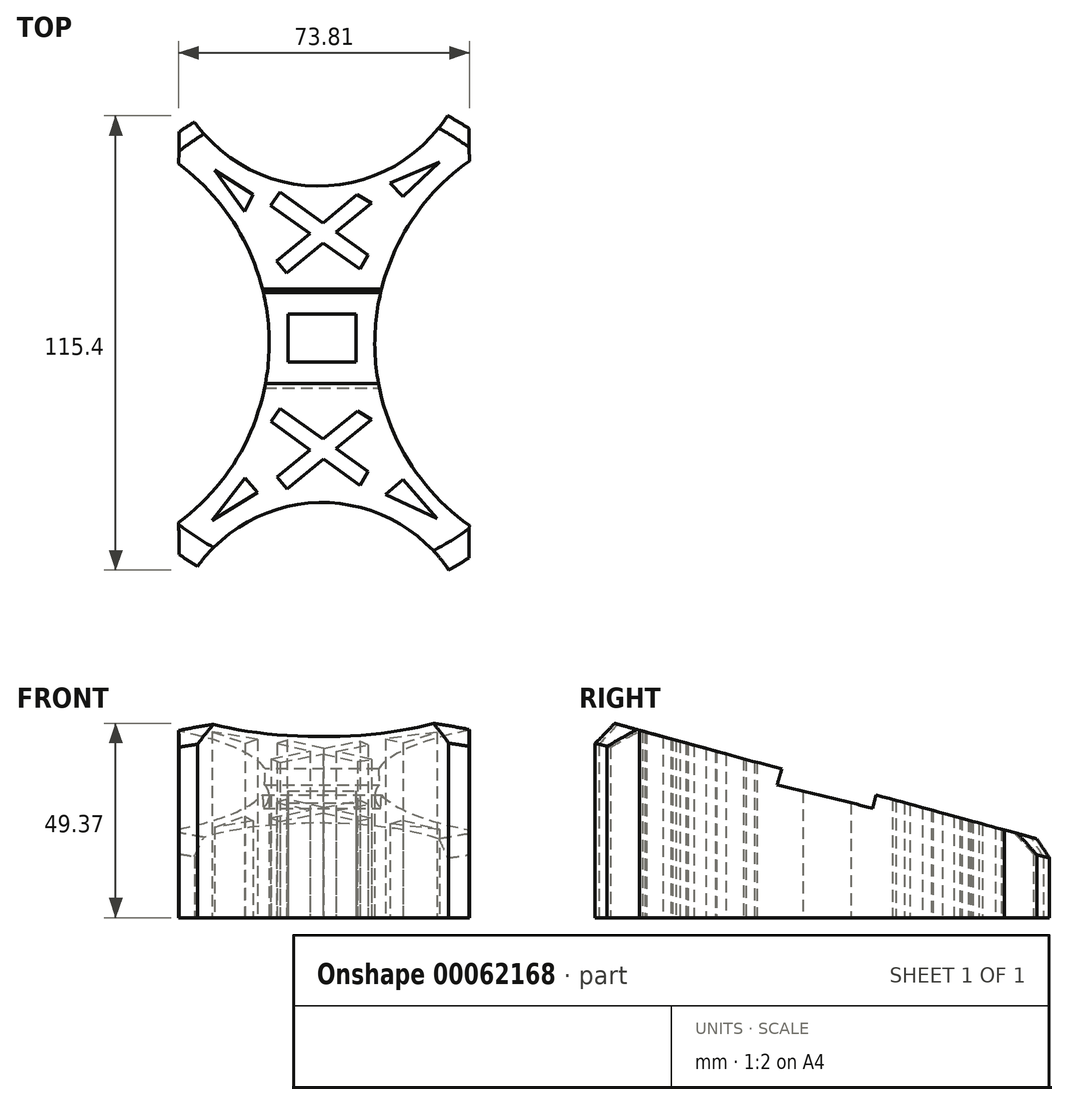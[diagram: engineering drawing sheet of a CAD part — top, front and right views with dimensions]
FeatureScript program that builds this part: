
annotation { "Feature Type Name" : "Feature", "Feature Type Description" : "" }
export const myFeature = defineFeature(function(context is Context, id is Id, definition is map)
    precondition{}
    {
        {
            var Q0;
            Q0=qCreatedBy(makeId("Top.planeOp"),FACE);
            var sketch = newSketch(context, id + "F0", { "sketchPlane" : qUnion([Q0])});
            skArc(sketch, "E0", {"start": v(-115.94, 56.2) * mm, "mid": v(-120.89, 52.92) * mm, "end": v(-125.52, 49.22) * mm});
            skArc(sketch, "E1", {"start": v(-40.14, 50) * mm, "mid": v(-70.11, 0) * mm, "end": v(-40.14, -50) * mm});
            skArc(sketch, "E2", {"start": v(-125.52, -49.22) * mm, "mid": v(-96.95, 0) * mm, "end": v(-125.52, 49.22) * mm});
            skArc(sketch, "E3", {"start": v(-115.94, 56.2) * mm, "mid": v(-83.36, 39.87) * mm, "end": v(-51.62, 57.78) * mm});
            skArc(sketch, "E4", {"start": v(-51.33, -57.62) * mm, "mid": v(-82.97, -40.44) * mm, "end": v(-115.1, -56.68) * mm});
            skArc(sketch, "E5.trimOffspring", {"start": v(-40.14, 50) * mm, "mid": v(-45.67, 54.2) * mm, "end": v(-51.62, 57.78) * mm});
            skArc(sketch, "E6.trimOffspring", {"start": v(-125.52, -49.22) * mm, "mid": v(-120.5, -53.2) * mm, "end": v(-115.1, -56.68) * mm});
            skArc(sketch, "E7.trimOffspring", {"start": v(-51.33, -57.62) * mm, "mid": v(-45.54, -54.1) * mm, "end": v(-40.14, -50) * mm});
            skSolve(sketch);
        }
        {
            var Q0;
            Q0 = qSketchRegion(id + "F0", true);
            extrude(context, id + "F1", {"entities" : qUnion([Q0]), "depth" : 50 * mm});
        }
        {
            var Q0;
            Q0=qCreatedBy(makeId("Right.planeOp"),FACE);
            var sketch = newSketch(context, id + "F2", { "sketchPlane" : qUnion([Q0])});
            skLineSegment(sketch, "E8", {"start": v(-59.85, 51.33) * mm, "end": v(61.8, 18.07) * mm});
            skLineSegment(sketch, "E9", {"start": v(61.8, 18.07) * mm, "end": v(61.8, 52.6) * mm});
            skLineSegment(sketch, "E10", {"start": v(61.8, 52.6) * mm, "end": v(-59.85, 51.33) * mm});
            skSolve(sketch);
        }
        {
            var Q0;
            Q0 = qSketchRegion(id + "F2", true);
            extrude(context, id + "F3", {"entities" : qUnion([Q0]), "operationType" : NewBodyOperationType.REMOVE, "endBound" : BoundingType.THROUGH_ALL, "oppositeDirection" : true, "depth" : 25 * mm});
        }
        {
            var Q0;
            Q0=qCreatedBy(makeId("Right.planeOp"),FACE);
            var sketch = newSketch(context, id + "F4", { "sketchPlane" : qUnion([Q0])});
            skLineSegment(sketch, "E11", {"start": v(-11.4, 33.8) * mm, "end": v(12.88, 27.84) * mm});
            skLineSegment(sketch, "E12", {"start": v(12.88, 27.84) * mm, "end": v(14.86, 35.9) * mm});
            skLineSegment(sketch, "E13", {"start": v(14.86, 35.9) * mm, "end": v(-9.04, 41.78) * mm});
            skLineSegment(sketch, "E14", {"start": v(-9.04, 41.78) * mm, "end": v(-11.4, 33.8) * mm});
            skSolve(sketch);
        }
        {
            var Q0;
            Q0 = qSketchRegion(id + "F4", true);
            extrude(context, id + "F5", {"entities" : qUnion([Q0]), "operationType" : NewBodyOperationType.REMOVE, "endBound" : BoundingType.THROUGH_ALL, "oppositeDirection" : true, "depth" : 25 * mm});
        }
        {
            var Q0;
            Q0=makeQuery(id+"F3.boolean.opBoolean","INTERSECT",EDGE,{"derivedFrom":[makeQuery(id+"F1.opExtrude","SWEPT_FACE",FACE,{"disambiguationData":[OSD([sQuery(id+"F0.wireOp",EDGE,"E0")])]}),makeQuery(id+"F3.opExtrude","SWEPT_FACE",FACE,{"disambiguationData":[OSD([sQuery(id+"F2.wireOp",EDGE,"E8")])]})]});
            var Q1;
            Q1=makeQuery(id+"F3.boolean.opBoolean","INTERSECT",EDGE,{"derivedFrom":[makeQuery(id+"F1.opExtrude","SWEPT_FACE",FACE,{"disambiguationData":[OSD([sQuery(id+"F0.wireOp",EDGE,"E5.trimOffspring")])]}),makeQuery(id+"F3.opExtrude","SWEPT_FACE",FACE,{"disambiguationData":[OSD([sQuery(id+"F2.wireOp",EDGE,"E8")])]})]});
            var Q2;
            Q2=makeQuery(id+"F3.boolean.opBoolean","INTERSECT",EDGE,{"derivedFrom":[makeQuery(id+"F1.opExtrude","SWEPT_FACE",FACE,{"disambiguationData":[OSD([sQuery(id+"F0.wireOp",EDGE,"E7.trimOffspring")])]}),makeQuery(id+"F3.opExtrude","SWEPT_FACE",FACE,{"disambiguationData":[OSD([sQuery(id+"F2.wireOp",EDGE,"E8")])]})]});
            var Q3;
            Q3=makeQuery(id+"F3.boolean.opBoolean","INTERSECT",EDGE,{"derivedFrom":[makeQuery(id+"F1.opExtrude","SWEPT_FACE",FACE,{"disambiguationData":[OSD([sQuery(id+"F0.wireOp",EDGE,"E6.trimOffspring")])]}),makeQuery(id+"F3.opExtrude","SWEPT_FACE",FACE,{"disambiguationData":[OSD([sQuery(id+"F2.wireOp",EDGE,"E8")])]})]});
            var Q4;
            Q4=makeQuery(id+"F1.opExtrude","SWEPT_EDGE",EDGE,{"disambiguationData":[OSD([sQuery(id+"F0.wireOp",EDGE,"E1"),sQuery(id+"F0.wireOp",EDGE,"E7.trimOffspring")])]});
            var Q5;
            Q5=makeQuery(id+"F1.opExtrude","SWEPT_EDGE",EDGE,{"disambiguationData":[OSD([sQuery(id+"F0.wireOp",EDGE,"E2"),sQuery(id+"F0.wireOp",EDGE,"E6.trimOffspring")])]});
            var Q6;
            Q6=makeQuery(id+"F1.opExtrude","SWEPT_EDGE",EDGE,{"disambiguationData":[OSD([sQuery(id+"F0.wireOp",EDGE,"E0"),sQuery(id+"F0.wireOp",EDGE,"E2")])]});
            var Q7;
            Q7=makeQuery(id+"F1.opExtrude","SWEPT_EDGE",EDGE,{"disambiguationData":[OSD([sQuery(id+"F0.wireOp",EDGE,"E1"),sQuery(id+"F0.wireOp",EDGE,"E5.trimOffspring")])]});
            chamfer(context, id + "F6", {"entities" : qUnion([Q0, Q1, Q2, Q3, Q4, Q5, Q6, Q7]), "width" : 5 * mm, "tangentPropagation" : true});
        }
        {
            var Q0;
            Q0=qCreatedBy(makeId("Top.planeOp"),FACE);
            var sketch = newSketch(context, id + "F7", { "sketchPlane" : qUnion([Q0])});
            skLineSegment(sketch, "E15.bottom", {"start": v(-92.17, 7.35) * mm, "end": v(-74.88, 7.35) * mm});
            skLineSegment(sketch, "E15.top", {"start": v(-92.17, -4.83) * mm, "end": v(-74.88, -4.83) * mm});
            skLineSegment(sketch, "E15.left", {"start": v(-92.17, 7.35) * mm, "end": v(-92.17, -4.83) * mm});
            skLineSegment(sketch, "E15.right", {"start": v(-74.88, 7.35) * mm, "end": v(-74.88, -4.83) * mm});
            skLineSegment(sketch, "E16", {"start": v(-96.58, 35) * mm, "end": v(-86.58, 27.85) * mm});
            skLineSegment(sketch, "E17", {"start": v(-71, 35.6) * mm, "end": v(-79.98, 28.17) * mm});
            skLineSegment(sketch, "E18", {"start": v(-92.49, 17.82) * mm, "end": v(-95.01, 20.88) * mm});
            skLineSegment(sketch, "E19", {"start": v(-95.01, 20.88) * mm, "end": v(-86.58, 27.85) * mm});
            skLineSegment(sketch, "E20", {"start": v(-74.62, 37.75) * mm, "end": v(-71, 35.6) * mm});
            skLineSegment(sketch, "E21", {"start": v(-96.58, 35) * mm, "end": v(-94.2, 38.34) * mm});
            skLineSegment(sketch, "E22", {"start": v(-94.2, 38.34) * mm, "end": v(-83.32, 30.55) * mm});
            skLineSegment(sketch, "E23", {"start": v(-71.86, 22.36) * mm, "end": v(-73.92, 18.8) * mm});
            skLineSegment(sketch, "E24.trimOffspring", {"start": v(-83.32, 30.55) * mm, "end": v(-74.62, 37.75) * mm});
            skLineSegment(sketch, "E25.trimOffspring", {"start": v(-79.98, 28.17) * mm, "end": v(-71.86, 22.36) * mm});
            skLineSegment(sketch, "E26.trimOffspring", {"start": v(-83.25, 25.46) * mm, "end": v(-92.49, 17.82) * mm});
            skLineSegment(sketch, "E27.trimOffspring", {"start": v(-83.25, 25.46) * mm, "end": v(-73.92, 18.8) * mm});
            skLineSegment(sketch, "E28", {"start": v(-70.93, -19.34) * mm, "end": v(-79.9, -26.77) * mm});
            skLineSegment(sketch, "E29.trimOffspring", {"start": v(-83.24, -24.38) * mm, "end": v(-74.54, -17.18) * mm});
            skLineSegment(sketch, "E30.trimOffspring", {"start": v(-83.18, -29.47) * mm, "end": v(-92.41, -37.11) * mm});
            skLineSegment(sketch, "E31.trimOffspring", {"start": v(-83.18, -29.47) * mm, "end": v(-73.85, -36.14) * mm});
            skLineSegment(sketch, "E32", {"start": v(-94.12, -16.6) * mm, "end": v(-83.24, -24.38) * mm});
            skLineSegment(sketch, "E33", {"start": v(-96.51, -19.93) * mm, "end": v(-86.51, -27.08) * mm});
            skLineSegment(sketch, "E34.trimOffspring", {"start": v(-79.9, -26.77) * mm, "end": v(-71.79, -32.58) * mm});
            skLineSegment(sketch, "E35", {"start": v(-94.94, -34.06) * mm, "end": v(-86.51, -27.08) * mm});
            skLineSegment(sketch, "E36", {"start": v(-96.51, -19.93) * mm, "end": v(-94.12, -16.6) * mm});
            skLineSegment(sketch, "E37", {"start": v(-92.41, -37.11) * mm, "end": v(-94.94, -34.06) * mm});
            skLineSegment(sketch, "E38", {"start": v(-71.79, -32.58) * mm, "end": v(-73.85, -36.14) * mm});
            skLineSegment(sketch, "E39", {"start": v(-74.54, -17.18) * mm, "end": v(-70.93, -19.34) * mm});
            skLineSegment(sketch, "E40", {"start": v(-110.82, 44.01) * mm, "end": v(-103.22, 33.5) * mm});
            skLineSegment(sketch, "E41", {"start": v(-103.22, 33.5) * mm, "end": v(-101.08, 37.78) * mm});
            skLineSegment(sketch, "E42", {"start": v(-101.08, 37.78) * mm, "end": v(-110.82, 44.01) * mm});
            skLineSegment(sketch, "E43", {"start": v(-66.22, 40.7) * mm, "end": v(-62.9, 37.2) * mm});
            skLineSegment(sketch, "E44", {"start": v(-62.9, 37.2) * mm, "end": v(-53.62, 45.97) * mm});
            skLineSegment(sketch, "E45", {"start": v(-53.62, 45.97) * mm, "end": v(-66.22, 40.7) * mm});
            skLineSegment(sketch, "E46", {"start": v(-103.03, -34.28) * mm, "end": v(-99.91, -37.99) * mm});
            skLineSegment(sketch, "E47", {"start": v(-99.91, -37.99) * mm, "end": v(-111.4, -45) * mm});
            skLineSegment(sketch, "E48", {"start": v(-111.4, -45) * mm, "end": v(-103.03, -34.28) * mm});
            skLineSegment(sketch, "E49", {"start": v(-67.36, -38.44) * mm, "end": v(-62.92, -34.58) * mm});
            skLineSegment(sketch, "E50", {"start": v(-62.92, -34.58) * mm, "end": v(-54.26, -44.55) * mm});
            skLineSegment(sketch, "E51", {"start": v(-54.26, -44.55) * mm, "end": v(-67.36, -38.44) * mm});
            skSolve(sketch);
        }
        {
            var Q0;
            Q0 = qSketchRegion(id + "F7", true);
            extrude(context, id + "F8", {"entities" : qUnion([Q0]), "operationType" : NewBodyOperationType.REMOVE, "endBound" : BoundingType.THROUGH_ALL, "depth" : 25 * mm});
        }
    });
